# Revit family: Platek_Menhir_1_Opening
name_source: partatom
category: Apparecchi per illuminazione
revit_build: Autodesk Revit 2017 (Build: 20160225_1515(x64)
units: mm (PartAtom-declared; Revit-internal decimal feet)

## family parameters
Basato su piano di lavoro = Sì
Condiviso = Sì
Punto di calcolo locali = No
Quota connettore circolare = Usa diametro
Sempre verticale = No
Sorgente d'illuminazione = Sì
Taglio con vuoti quando caricato = No
Tipo di parte = Normale

## types (3) — shared parameters
Beam Angle = 0.00°
Body = PLK_Grey
CRI = >80
Carico apparente = 0 VA
Colour Temperature = 3000 K
Commenti sul tipo = Pedestrian areas, Urban zones, Paths, Roads
Descrizione = Outdoor Lighting, Floor/Ground Illumination
Diffuse Type = PMMA
Dimmable = No
Emetti da diametro cerchio = 1 mm  [stored 0.00328084 ft]
Energy Efficiency Rating = A/A+/A++
Filtro dei colori = 16777215
Frequency = 50/60 Hz
IK Rating = IK08
IP Rating = IP65
Insulation Class = 1
LED Protection = Surge protection included
Lampada = LED
Light Source = PLK_Light Source
Modello = MENHIR
Mounting Type = Ground
Nota chiave = Other Led colors available on request
PLATEK FInishes = Painted Aluminium Avalaible in Anthracite/Black/White/Corten/Bronze
Power Supply Unit = Included
Product Documentation Link = http://www.platek.eu
Product Page URL = http://www.platek.eu
Produttore = PLATEK SRL
Prospetto di default = 1219.2 mm  [stored 4 ft]
Rendi la forma visibile nel rendering = No
Supply Voltage = 230 V
Supply Voltage Max = 240 V
Supply Voltage Min = 220 V
URL = www.platek.eu
Variazione temperatura colore lampada con luminosità attenuata = <Nessuno>

## per-type parameters (varying)
| type | Aluminium | Angolo inclinazione | Cable Lenght | Codice assieme | File diagramma fotometrico | Height | Height1050 | Height200 | Height620 | Immagine tipo | Luminaire Luminous Flux | Luminaire Luminous Intensity | Luminaire Wattage | Manufacturer Comment | PLATEK Article Code | Product Dimension |
| 4032611_15,3W_LED_3000K_H200mm | PLK_Aluminium | 45.00° | Ø4,5÷10mm | 4032611.06(Grey); 4032611.08(Anthracite); 4032611.01(Black); 4032611.02(White); 4032611.07(Corten); 4032611.09(Bronze) | 4032611.IES | 210 mm  [stored 0.688976 ft] | No | Sì | No | menhir_led_dim1.jpg | 510 lm | 389 cd | 15 W | 5mm Thick PMMA | 4032611 | D200mm x H200mm |
| 4052611_20,3W_LED_3000K_H620mm | PLK_Light Source | 90.00° | 1m (3x1mm^2) | 4052611.06(Grey); 4052611.08(Anthracite); 4052611.01(Black); 4052611.02(White); 4052611.07(Corten); 4052611.09(Bronze) | 4052611.IES | 620 mm  [stored 2.03412 ft] | No | No | Sì | menhir_led_dim2.jpg | 775 lm | 591 cd | 20 W | 4mmThick PMMA | 4052611 | D200mm x H620mm |
| 4082611_40,2W_LED_3000K_H1050mm | PLK_Aluminium | 90.00° | 1,5m (3x1mm^2) | 4082611.06(Grey); 4082611.08(Anthracite); 4082611.01(Black); 4082611.02(White); 4082611.07(Corten); 4082611.09(Bronze) | 4082611.IES | 1050 mm | Sì | No | No | menhir_led_dim3.jpg | 1433 lm | 1093 cd | 40 W | 4mm Thick PMMA | 4082611 | D200mm x H1050mm |

note: [stored X ft] marks values corroborated as IEEE doubles in the binary element streams (Revit-internal decimal feet)
